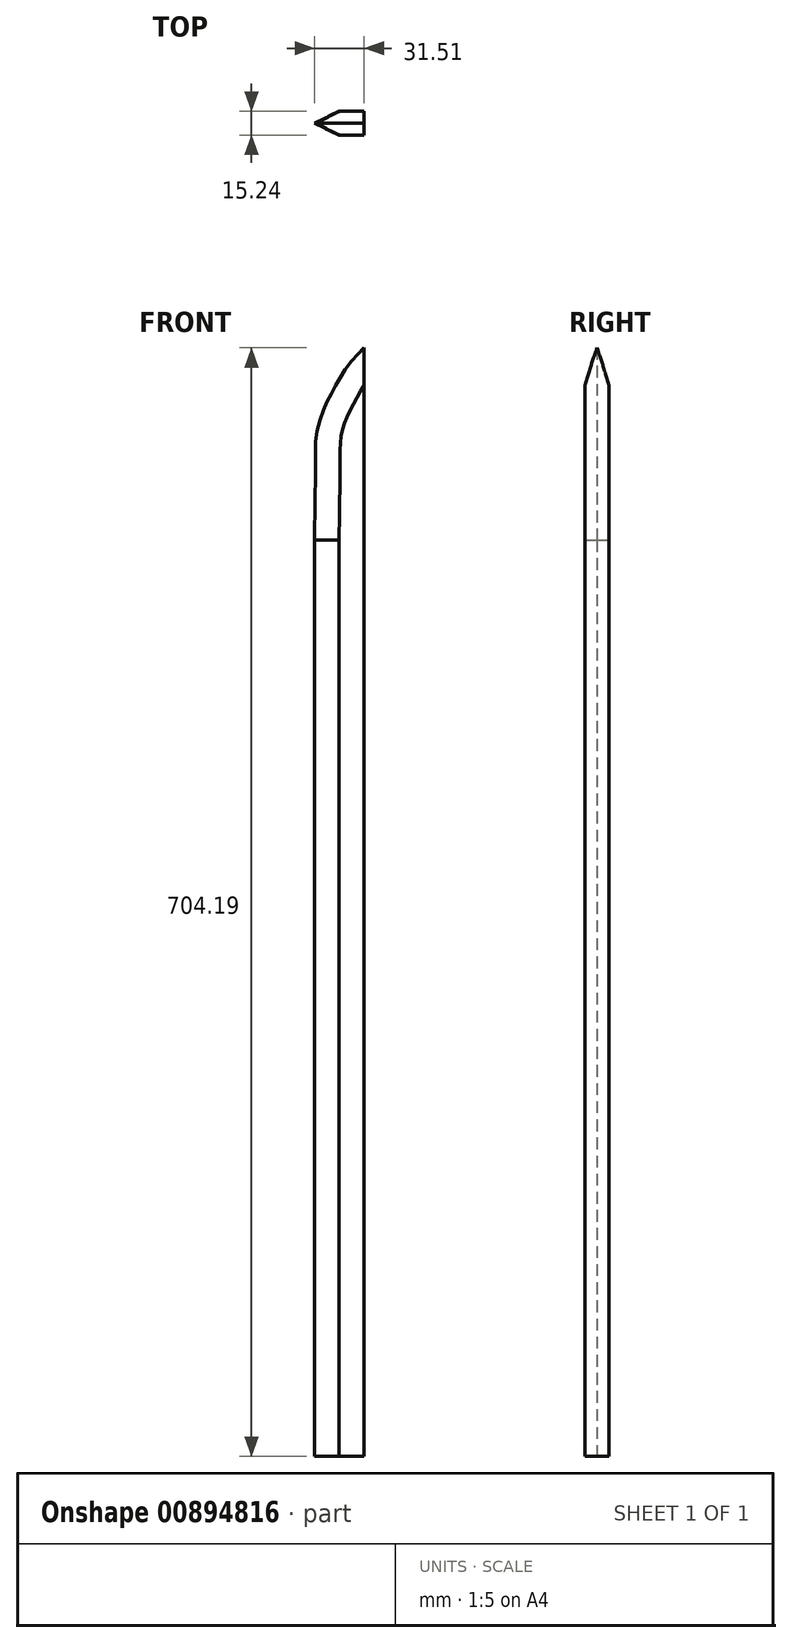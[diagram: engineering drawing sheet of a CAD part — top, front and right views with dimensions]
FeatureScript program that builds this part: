
annotation { "Feature Type Name" : "Feature", "Feature Type Description" : "" }
export const myFeature = defineFeature(function(context is Context, id is Id, definition is map)
    precondition{}
    {
        {
            var Q0;
            Q0=qCreatedBy(makeId("Front.planeOp"),FACE);
            var sketch = newSketch(context, id + "F0", { "sketchPlane" : qUnion([Q0])});
            skLineSegment(sketch, "E0", {"start": v(-12.43, 147.36) * mm, "end": v(-12.43, 694.5) * mm});
            skLineSegment(sketch, "E1", {"start": v(19.08, 182.02) * mm, "end": v(19.08, 816.67) * mm});
            skLineSegment(sketch, "E2", {"start": v(-12.43, 147.36) * mm, "end": v(-12.43, 112.48) * mm});
            skLineSegment(sketch, "E3", {"start": v(19.08, 182.02) * mm, "end": v(19.08, 112.48) * mm});
            skLineSegment(sketch, "E4", {"start": v(19.08, 112.48) * mm, "end": v(-12.43, 112.48) * mm});
            skFitSpline(sketch, "E5", {"points": [v(19.08, 816.67) * mm, v(9, 805.47) * mm, v(0, 790.9) * mm, v(-10.04, 767.38) * mm, v(-11.9, 747.6) * mm, v(-11.9, 730.42) * mm, v(-12.43, 694.5) * mm], "startDerivative": vector(-75.25, -77.3) * mm, "endDerivative": vector(-3.24, -182.15) * mm});
            skSolve(sketch);
        }
        {
            var Q0;
            Q0=makeQuery(id+"F0.imprint","IMPRINT",FACE,{"disambiguationData":[TD([[makeQuery(id+"F0.imprint","IMPRINT",EDGE,{"derivedFrom":sQuery(id+"F0.wireOp",EDGE,"E0")}),-1.0]])]});
            extrude(context, id + "F1", {"entities" : qUnion([Q0]), "depth" : 7.62 * mm, "offsetDistance" : 25.4 * mm});
        }
        {
            var Q0;
            Q0=makeQuery(id+"F1.opExtrude","CAP_FACE",FACE,{"disambiguationData":[OSD([sQuery(id+"F0.wireOp",EDGE,"E0"),sQuery(id+"F0.wireOp",EDGE,"E1"),sQuery(id+"F0.wireOp",EDGE,"55b54924-0589-4df6-90b1-72972e55ac43"),sQuery(id+"F0.wireOp",EDGE,"E2"),sQuery(id+"F0.wireOp",EDGE,"E3"),sQuery(id+"F0.wireOp",EDGE,"E4")])],"isStart":true});
            extrude(context, id + "F2", {"entities" : qUnion([Q0]), "operationType" : NewBodyOperationType.ADD, "depth" : 7.62 * mm, "offsetDistance" : 25.4 * mm});
        }
        {
            var Q0;
            Q0=makeQuery(id+"F2.opExtrude","CAP_EDGE",EDGE,{"disambiguationData":[OSD([sQuery(id+"F0.wireOp",EDGE,"E5")])],"isStart":false});
            var Q1;
            Q1=makeQuery(id+"F1.opExtrude","CAP_EDGE",EDGE,{"disambiguationData":[OSD([sQuery(id+"F0.wireOp",EDGE,"E5")])],"isStart":false});
            var Q2;
            Q2=makeQuery(id+"F1.opExtrude","CAP_EDGE",EDGE,{"disambiguationData":[OSD([sQuery(id+"F0.wireOp",EDGE,"E0"),sQuery(id+"F0.wireOp",EDGE,"E2")])],"isStart":false});
            var Q3;
            Q3=makeQuery(id+"F2.opExtrude","CAP_EDGE",EDGE,{"disambiguationData":[OSD([sQuery(id+"F0.wireOp",EDGE,"E0"),sQuery(id+"F0.wireOp",EDGE,"E2")])],"isStart":false});
            chamfer(context, id + "F3", {"entities" : qUnion([Q0, Q1, Q2, Q3]), "chamferType" : ChamferType.OFFSET_ANGLE, "width" : 7.62 * mm, "oppositeDirection" : false, "angle" : 64 * degree, "tangentPropagation" : true});
        }
    });
